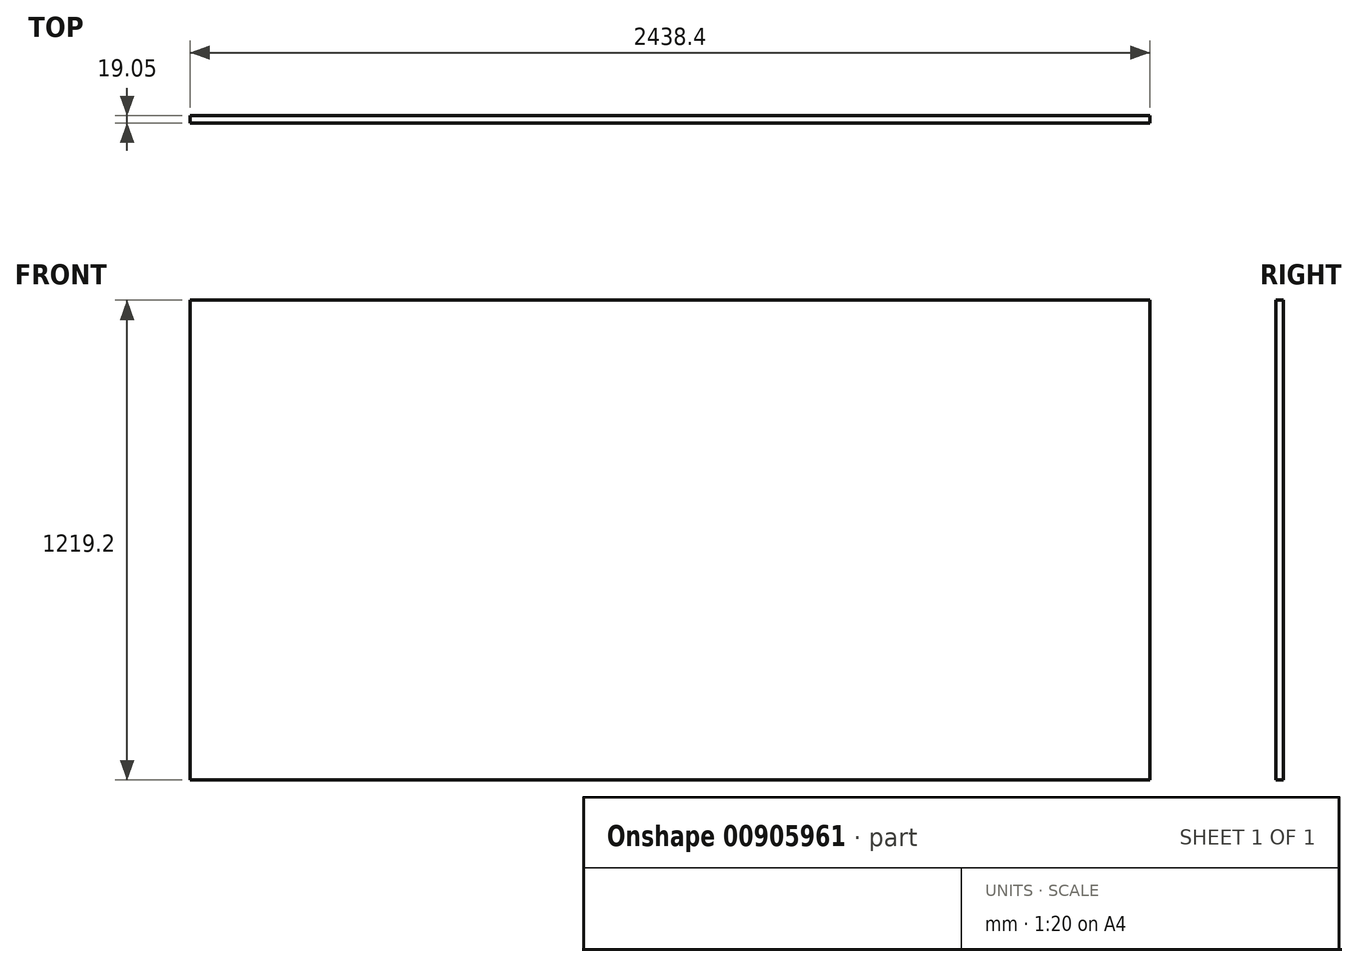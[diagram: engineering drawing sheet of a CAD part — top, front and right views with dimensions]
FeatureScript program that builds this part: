
annotation { "Feature Type Name" : "Feature", "Feature Type Description" : "" }
export const myFeature = defineFeature(function(context is Context, id is Id, definition is map)
    precondition{}
    {
        {
            var Q0;
            Q0=qCreatedBy(makeId("Front.planeOp"),FACE);
            var sketch = newSketch(context, id + "F0", { "sketchPlane" : qUnion([Q0])});
            skLineSegment(sketch, "E0.bottom", {"start": v(0, 0) * mm, "end": v(2438.4, 0) * mm});
            skLineSegment(sketch, "E0.top", {"start": v(0, 1219.2) * mm, "end": v(2438.4, 1219.2) * mm});
            skLineSegment(sketch, "E0.left", {"start": v(0, 0) * mm, "end": v(0, 1219.2) * mm});
            skLineSegment(sketch, "E0.right", {"start": v(2438.4, 0) * mm, "end": v(2438.4, 1219.2) * mm});
            skSolve(sketch);
        }
        {
            var Q0;
            Q0=makeQuery(id+"F0.imprint","IMPRINT",FACE,{"disambiguationData":[TD([[makeQuery(id+"F0.imprint","IMPRINT",EDGE,{"derivedFrom":sQuery(id+"F0.wireOp",EDGE,"E0.bottom")}),1.0]])]});
            extrude(context, id + "F1", {"entities" : qUnion([Q0]), "depth" : 19.05 * mm, "offsetDistance" : 25.4 * mm});
        }
    });
